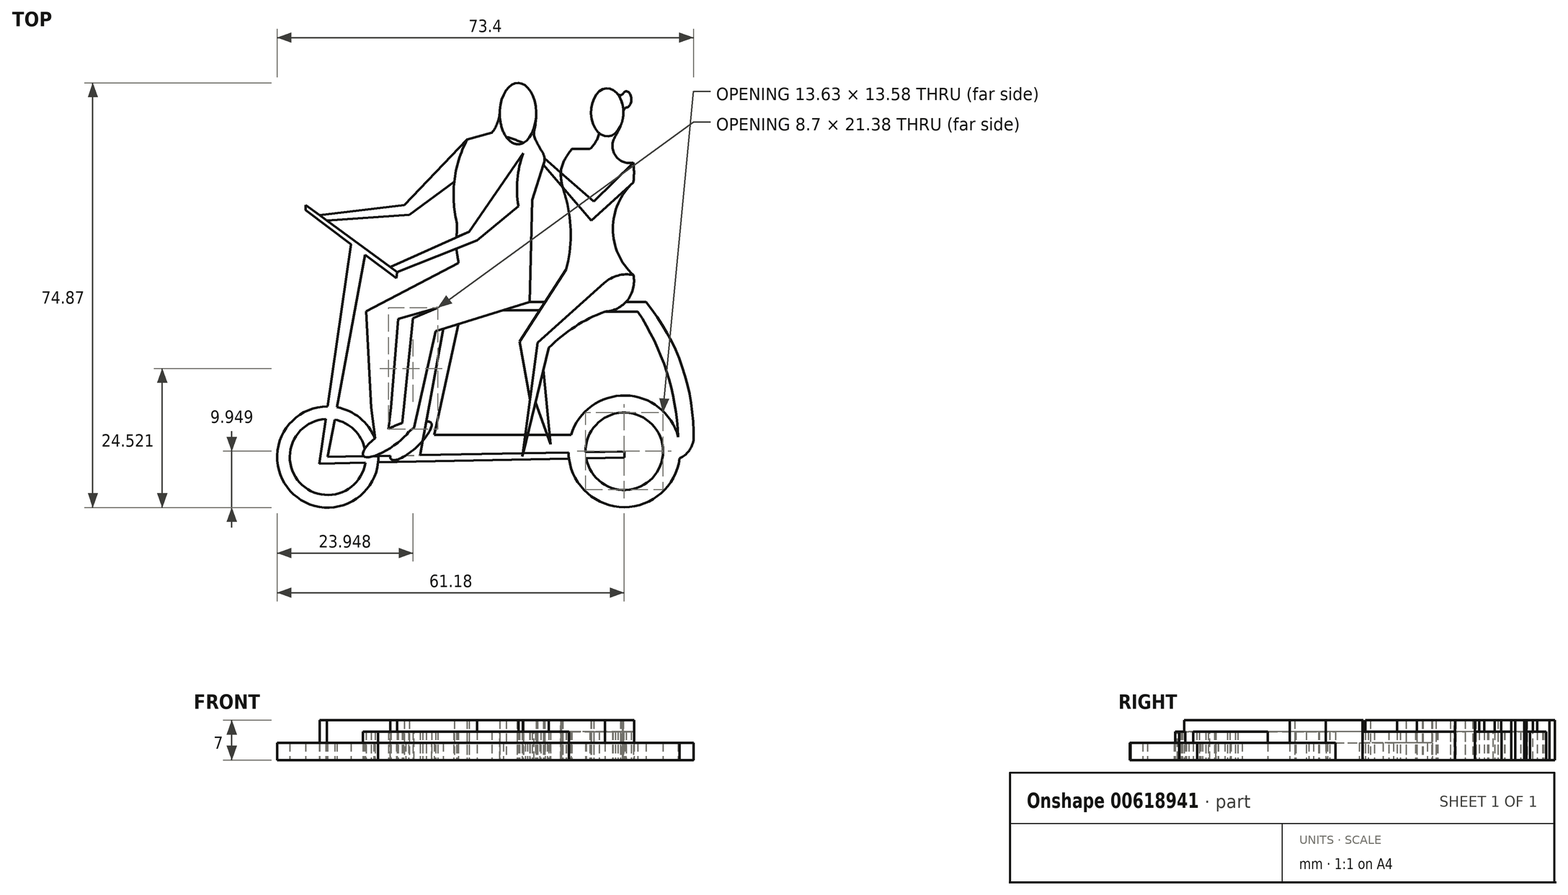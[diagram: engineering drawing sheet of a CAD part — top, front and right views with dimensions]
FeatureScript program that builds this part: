
annotation { "Feature Type Name" : "Feature", "Feature Type Description" : "" }
export const myFeature = defineFeature(function(context is Context, id is Id, definition is map)
    precondition{}
    {
        {
            var Q0;
            Q0=qCreatedBy(makeId("Top.planeOp"),FACE);
            var sketch = newSketch(context, id + "F0", { "sketchPlane" : qUnion([Q0])});
            skLineSegment(sketch, "E0", {"start": v(-116.6, -48.98) * mm, "end": v(-114.7, -48.98) * mm});
            skArc(sketch, "E1", {"start": v(-94.37, -13.85) * mm, "mid": v(-94.25, -12.1) * mm, "end": v(-94.37, -10.37) * mm});
            skArc(sketch, "E2", {"start": v(-97.5, -5.68) * mm, "mid": v(-97.53, -9.1) * mm, "end": v(-94.37, -10.37) * mm});
            skLineSegment(sketch, "E3", {"start": v(-97.5, -5.68) * mm, "end": v(-100.18, -3.95) * mm});
            skPoint(sketch, "E4.startSnap0", {"position": v(-116.27, -23.85) * mm});
            skPoint(sketch, "E5.startSnap0", {"position": v(-110.08, -34.92) * mm});
            skPoint(sketch, "E6.endSnap0", {"position": v(-97.53, -9.1) * mm});
            skArc(sketch, "E7", {"start": v(-99.4, -36.63) * mm, "mid": v(-95.38, -34.57) * mm, "end": v(-94.37, -30.19) * mm});
            skPoint(sketch, "E8.endSnap0", {"position": v(-107.17, -42.99) * mm});
            skPoint(sketch, "E9.startSnap0", {"position": v(-109.77, -40.6) * mm});
            skLineSegment(sketch, "E10", {"start": v(-109.25, -42.99) * mm, "end": v(-113.94, -62.2) * mm});
            skLineSegment(sketch, "E11", {"start": v(-99.5, -31.56) * mm, "end": v(-111.26, -42.09) * mm});
            skLineSegment(sketch, "E12", {"start": v(-111.26, -42.09) * mm, "end": v(-113.94, -62.2) * mm});
            skLineSegment(sketch, "E13", {"start": v(-106.24, -29.19) * mm, "end": v(-114.45, -41.92) * mm});
            skLineSegment(sketch, "E14", {"start": v(-114.45, -41.92) * mm, "end": v(-112.6, -52.14) * mm});
            skLineSegment(sketch, "E15", {"start": v(-111.6, -52.59) * mm, "end": v(-108.96, -60) * mm});
            skLineSegment(sketch, "E16", {"start": v(-108.96, -60) * mm, "end": v(-110.2, -46.86) * mm});
            skLineSegment(sketch, "E17", {"start": v(-101.78, -20.58) * mm, "end": v(-94.37, -13.85) * mm});
            skLineSegment(sketch, "E18", {"start": v(-94.37, -10.37) * mm, "end": v(-101.35, -17.21) * mm});
            skPoint(sketch, "E18.endSnap0", {"position": v(-98.08, -17.21) * mm});
            skLineSegment(sketch, "E19", {"start": v(-101.35, -17.21) * mm, "end": v(-110.02, -9.6) * mm});
            skArc(sketch, "E20", {"start": v(-99.4, -36.63) * mm, "mid": v(-104.67, -39.27) * mm, "end": v(-109.25, -42.99) * mm});
            skArc(sketch, "E21", {"start": v(-94.37, -13.85) * mm, "mid": v(-97.98, -22.02) * mm, "end": v(-94.37, -30.19) * mm});
            skFitSpline(sketch, "E22", {"points": [v(-105.2, -7.94) * mm, v(-107.16, -12.1) * mm, v(-106.18, -16.95) * mm], "startDerivative": vector(-6.26, -8.42) * mm, "endDerivative": vector(2.06, -8.25) * mm});
            skArc(sketch, "E23", {"start": v(-106.24, -29.19) * mm, "mid": v(-105.4, -23.07) * mm, "end": v(-106.18, -16.95) * mm});
            skLineSegment(sketch, "E24", {"start": v(-105.2, -7.94) * mm, "end": v(-102.02, -7.94) * mm});
            skArc(sketch, "E25", {"start": v(-102.02, -7.94) * mm, "mid": v(-100.7, -6.13) * mm, "end": v(-100.18, -3.95) * mm});
            skLineSegment(sketch, "E26", {"start": v(-112.66, -7.26) * mm, "end": v(-113.8, -8.71) * mm});
            skArc(sketch, "E27", {"start": v(-123.67, -6.32) * mm, "mid": v(-125.9, -13.41) * mm, "end": v(-125.5, -20.84) * mm});
            skArc(sketch, "E28", {"start": v(-113.8, -8.71) * mm, "mid": v(-114.89, -14.53) * mm, "end": v(-114.05, -20.4) * mm});
            skFitSpline(sketch, "E29", {"points": [v(-125.5, -20.84) * mm, v(-125.5, -22.87) * mm, v(-125.5, -25.98) * mm, v(-125.5, -30.56) * mm, v(-128, -34.92) * mm], "startDerivative": vector(1.3, -15.74) * mm, "endDerivative": vector(3.93, -16.51) * mm});
            skFitSpline(sketch, "E30", {"points": [v(-114.05, -20.4) * mm, v(-114.4, -23.72) * mm, v(-114.05, -27.05) * mm, v(-114.4, -29.84) * mm, v(-114.05, -34.92) * mm], "startDerivative": vector(0, -14.22) * mm, "endDerivative": vector(0, -18.32) * mm});
            skLineSegment(sketch, "E31", {"start": v(-114.4, -29.84) * mm, "end": v(-133.21, -37.8) * mm});
            skLineSegment(sketch, "E32", {"start": v(-133.21, -37.8) * mm, "end": v(-134.84, -53.98) * mm});
            skLineSegment(sketch, "E33", {"start": v(-132.34, -53.98) * mm, "end": v(-129.2, -40.08) * mm});
            skLineSegment(sketch, "E34", {"start": v(-129.2, -40.08) * mm, "end": v(-112.66, -34.92) * mm});
            skLineSegment(sketch, "E35", {"start": v(-125.18, -28.08) * mm, "end": v(-141.44, -36.6) * mm});
            skLineSegment(sketch, "E36", {"start": v(-141.44, -36.6) * mm, "end": v(-140.6, -53.55) * mm});
            skLineSegment(sketch, "E37", {"start": v(-137.12, -53.55) * mm, "end": v(-135.82, -37.9) * mm});
            skLineSegment(sketch, "E38", {"start": v(-135.82, -37.9) * mm, "end": v(-128.86, -35.96) * mm});
            skArc(sketch, "E39", {"start": v(-112.66, -7.26) * mm, "mid": v(-115.95, -6.08) * mm, "end": v(-119.3, -5.1) * mm});
            skPoint(sketch, "E40.endSnap0", {"position": v(-114.89, -14.53) * mm});
            skLineSegment(sketch, "E41", {"start": v(-112.66, -34.92) * mm, "end": v(-92.15, -34.92) * mm});
            skLineSegment(sketch, "E42", {"start": v(-125.22, -38.84) * mm, "end": v(-129.2, -57.18) * mm});
            skArc(sketch, "E43", {"start": v(-83.78, -59.33) * mm, "mid": v(-85.75, -46.36) * mm, "end": v(-92.15, -34.92) * mm});
            skPoint(sketch, "E44.endSnap0", {"position": v(-145, -40.91) * mm});
            skLineSegment(sketch, "E45", {"start": v(-128.94, -58.34) * mm, "end": v(-113.43, -58.34) * mm});
            skLineSegment(sketch, "E46", {"start": v(-123.67, -6.32) * mm, "end": v(-119.3, -5.1) * mm});
            skLineSegment(sketch, "E47", {"start": v(-152.12, -17.86) * mm, "end": v(-136.02, -29.67) * mm});
            skLineSegment(sketch, "E48", {"start": v(-121.92, -24.08) * mm, "end": v(-136.02, -29.67) * mm});
            skLineSegment(sketch, "E49", {"start": v(-123.32, -22.52) * mm, "end": v(-113.8, -8.71) * mm});
            skLineSegment(sketch, "E50", {"start": v(-149.68, -19.65) * mm, "end": v(-134.77, -17.86) * mm});
            skLineSegment(sketch, "E51", {"start": v(-134.77, -17.86) * mm, "end": v(-123.67, -6.32) * mm});
            skLineSegment(sketch, "E52", {"start": v(-133.87, -19.52) * mm, "end": v(-124.02, -12.3) * mm});
            skCircle(sketch, "E53", {"center": v(-148.23, -62.25) * mm, "radius": 8.92 * mm});
            skCircle(sketch, "E54", {"center": v(-95.96, -61.25) * mm, "radius": 9.84 * mm});
            skLineSegment(sketch, "E55", {"start": v(-148.23, -62.25) * mm, "end": v(-95.96, -61.25) * mm});
            skLineSegment(sketch, "E56", {"start": v(-129.2, -57.18) * mm, "end": v(-129.45, -58.34) * mm});
            skLineSegment(sketch, "E57", {"start": v(-129.45, -58.34) * mm, "end": v(-128.94, -58.34) * mm});
            skArc(sketch, "E58", {"start": v(-89.73, -62.43) * mm, "mid": v(-85.97, -62.39) * mm, "end": v(-83.78, -59.33) * mm});
            skEllipse(sketch, "E59", {"center": v(-114.71, -1.7) * mm, "majorRadius": 5.4 * mm, "minorRadius": 3.2 * mm, "majorAxis": v(0, -1)});
            skArc(sketch, "E60", {"start": v(-119.3, -5.1) * mm, "mid": v(-118.29, -3.24) * mm, "end": v(-117.9, -1.16) * mm});
            skLineSegment(sketch, "E61", {"start": v(-97.98, 0) * mm, "end": v(-97.98, -1.77) * mm});
            skEllipse(sketch, "E62", {"center": v(-98.97, -1.48) * mm, "majorRadius": 4.24 * mm, "minorRadius": 2.85 * mm, "majorAxis": v(0, -1)});
            skEllipse(sketch, "E63", {"center": v(-95.61, 0.8) * mm, "majorRadius": 1.42 * mm, "minorRadius": 0.88 * mm, "majorAxis": v(0, -1)});
            skArc(sketch, "E64", {"start": v(-97.1, 1.72) * mm, "mid": v(-96.52, 1.56) * mm, "end": v(-96.1, 1.99) * mm});
            skArc(sketch, "E65", {"start": v(-95.61, -0.63) * mm, "mid": v(-96.04, -1.07) * mm, "end": v(-96.12, -1.7) * mm});
            skPoint(sketch, "E66.2.internal.snap0", {"position": v(-94.73, 0.8) * mm});
            skArc(sketch, "E67", {"start": v(-95.54, -5.6) * mm, "mid": v(-96.7, -5.3) * mm, "end": v(-97.9, -5.42) * mm});
            skLineSegment(sketch, "E68", {"start": v(-149.75, -63.42) * mm, "end": v(-95.96, -62.33) * mm});
            skLineSegment(sketch, "E69", {"start": v(-95.96, -62.33) * mm, "end": v(-95.96, -61.25) * mm});
            skLineSegment(sketch, "E70", {"start": v(-152.12, -17.86) * mm, "end": v(-152.12, -18.73) * mm});
            skLineSegment(sketch, "E71", {"start": v(-152.12, -18.73) * mm, "end": v(-136.11, -30.76) * mm});
            skLineSegment(sketch, "E72", {"start": v(-136.11, -30.76) * mm, "end": v(-136.02, -29.67) * mm});
            skCircle(sketch, "E73", {"center": v(-148.23, -62.25) * mm, "radius": 6.7 * mm});
            skCircle(sketch, "E74", {"center": v(-95.96, -61.25) * mm, "radius": 6.83 * mm});
            skLineSegment(sketch, "E75", {"start": v(-137.24, -28.77) * mm, "end": v(-123.32, -22.52) * mm});
            skLineSegment(sketch, "E76", {"start": v(-133.87, -19.52) * mm, "end": v(-148.42, -20.57) * mm});
            skLineSegment(sketch, "E77", {"start": v(-113, -58.34) * mm, "end": v(-105.36, -58.34) * mm});
            skLineSegment(sketch, "E78", {"start": v(-148.23, -62.25) * mm, "end": v(-141.66, -26.59) * mm});
            skLineSegment(sketch, "E79", {"start": v(-149.75, -63.42) * mm, "end": v(-144.11, -24.74) * mm});
            skLineSegment(sketch, "E80", {"start": v(-110.02, -10.17) * mm, "end": v(-112.2, -16.92) * mm});
            skLineSegment(sketch, "E81", {"start": v(-112.2, -16.92) * mm, "end": v(-112.66, -34.92) * mm});
            skArc(sketch, "E82", {"start": v(-110.02, -10.17) * mm, "mid": v(-110.68, -8.12) * mm, "end": v(-112.66, -7.26) * mm});
            skLineSegment(sketch, "E83", {"start": v(-101.78, -20.58) * mm, "end": v(-110.2, -10.75) * mm});
            skLineSegment(sketch, "E84", {"start": v(-117.29, -36.37) * mm, "end": v(-110.86, -36.37) * mm});
            skLineSegment(sketch, "E85", {"start": v(-99.4, -36.63) * mm, "end": v(-93.58, -36.63) * mm});
            skArc(sketch, "E86", {"start": v(-86.46, -58.72) * mm, "mid": v(-88.51, -47.19) * mm, "end": v(-93.58, -36.63) * mm});
            skLineSegment(sketch, "E87", {"start": v(-127.85, -39.66) * mm, "end": v(-131.96, -61.94) * mm});
            skArc(sketch, "E88", {"start": v(-94.37, -30.19) * mm, "mid": v(-97.1, -30.26) * mm, "end": v(-99.5, -31.56) * mm});
            skLineSegment(sketch, "E89", {"start": v(-121.92, -24.08) * mm, "end": v(-114.63, -18) * mm});
            skFitSpline(sketch, "E90", {"points": [v(-111.52, -2.3) * mm, v(-111.87, -5.2) * mm, v(-111.54, -6.5) * mm, v(-110.68, -8.12) * mm], "startDerivative": vector(-0.02, -8.02) * mm, "endDerivative": vector(2.84, -6.3) * mm});
            skArc(sketch, "E91", {"start": v(-97.5, -5.68) * mm, "mid": v(-96.9, -4.5) * mm, "end": v(-96.38, -3.27) * mm});
            skLineSegment(sketch, "E92", {"start": v(-140.6, -53.55) * mm, "end": v(-139.84, -59.24) * mm});
            skLineSegment(sketch, "E93", {"start": v(-137.12, -53.55) * mm, "end": v(-137.78, -59.24) * mm});
            skLineSegment(sketch, "E94", {"start": v(-134.84, -53.98) * mm, "end": v(-135.53, -59.19) * mm});
            skLineSegment(sketch, "E95", {"start": v(-132.34, -53.98) * mm, "end": v(-133.57, -59.41) * mm});
            skPoint(sketch, "E96.0.internal.snap0", {"position": v(-134.27, -61.65) * mm});
            skEllipse(sketch, "E97", {"center": v(-133.57, -59.41) * mm, "majorRadius": 4.77 * mm, "minorRadius": 1.46 * mm, "majorAxis": v(-0.73, -0.68)});
            skEllipse(sketch, "E98", {"center": v(-137.78, -59.24) * mm, "majorRadius": 5.05 * mm, "minorRadius": 1.5 * mm, "majorAxis": v(-0.83, -0.55)});
            skArc(sketch, "E99", {"start": v(-107.16, -12.1) * mm, "mid": v(-107.07, -13.42) * mm, "end": v(-106.8, -14.72) * mm});
            skSolve(sketch);
        }
        {
            var Q0;
            {var subQ0=sQuery(id+"F0.wireOp",EDGE,"E79");var subQ1=sQuery(id+"F0.wireOp",EDGE,"E53");var subQ2=makeQuery(id+"F0.imprint","INTERSECT",VERTEX,{"derivedFrom":[subQ1,subQ0]});Q0=makeQuery(id+"F0.imprint","IMPRINT",FACE,{"disambiguationData":[TD([[makeQuery(id+"F0.imprint","IMPRINT",EDGE,{"disambiguationData":[TD([[subQ2,1.0]])],"derivedFrom":subQ1}),-1.0]])]});}
            var Q1;
            {var subQ0=sQuery(id+"F0.wireOp",EDGE,"E79");var subQ1=sQuery(id+"F0.wireOp",EDGE,"E53");var subQ2=makeQuery(id+"F0.imprint","INTERSECT",VERTEX,{"derivedFrom":[subQ1,subQ0]});Q1=makeQuery(id+"F0.imprint","IMPRINT",FACE,{"disambiguationData":[TD([[makeQuery(id+"F0.imprint","IMPRINT",EDGE,{"disambiguationData":[TD([[subQ2,1.0]])],"derivedFrom":subQ1}),1.0]])]});}
            var Q2;
            {var subQ0=sQuery(id+"F0.wireOp",EDGE,"E79");var subQ1=sQuery(id+"F0.wireOp",EDGE,"E53");var subQ2=makeQuery(id+"F0.imprint","INTERSECT",VERTEX,{"derivedFrom":[subQ1,subQ0]});Q2=makeQuery(id+"F0.imprint","IMPRINT",FACE,{"disambiguationData":[TD([[makeQuery(id+"F0.imprint","IMPRINT",EDGE,{"disambiguationData":[TD([[subQ2,-1.0]])],"derivedFrom":subQ1}),1.0]])]});}
            var Q3;
            {var subQ0=sQuery(id+"F0.wireOp",EDGE,"E78");var subQ1=sQuery(id+"F0.wireOp",EDGE,"E53");var subQ2=makeQuery(id+"F0.imprint","INTERSECT",VERTEX,{"derivedFrom":[subQ1,subQ0]});Q3=makeQuery(id+"F0.imprint","IMPRINT",FACE,{"disambiguationData":[TD([[makeQuery(id+"F0.imprint","IMPRINT",EDGE,{"disambiguationData":[TD([[subQ2,1.0]])],"derivedFrom":subQ1}),1.0]])]});}
            var Q4;
            {var subQ1=sQuery(id+"F0.wireOp",EDGE,"E55");var subQ7=sQuery(id+"F0.wireOp",EDGE,"E78");var subQ10=makeQuery(id+"F0.imprint","INTERSECT",VERTEX,{"derivedFrom":[subQ1,subQ7]});Q4=makeQuery(id+"F0.imprint","IMPRINT",FACE,{"disambiguationData":[TD([[makeQuery(id+"F0.imprint","IMPRINT",EDGE,{"disambiguationData":[TD([[subQ10,-1.0]])],"derivedFrom":subQ1}),-1.0]])]});}
            var Q5;
            {var subQ0=sQuery(id+"F0.wireOp",EDGE,"E68");var subQ1=sQuery(id+"F0.wireOp",EDGE,"E53");var subQ2=makeQuery(id+"F0.imprint","INTERSECT",VERTEX,{"derivedFrom":[subQ1,subQ0]});Q5=makeQuery(id+"F0.imprint","IMPRINT",FACE,{"disambiguationData":[TD([[makeQuery(id+"F0.imprint","IMPRINT",EDGE,{"disambiguationData":[TD([[subQ2,-1.0]])],"derivedFrom":subQ1}),1.0]])]});}
            var Q6;
            {var subQ7=sQuery(id+"F0.wireOp",EDGE,"E70");Q6=makeQuery(id+"F0.imprint","IMPRINT",FACE,{"disambiguationData":[TD([[makeQuery(id+"F0.imprint","IMPRINT",EDGE,{"derivedFrom":subQ7}),1.0]])]});}
            var Q7;
            {var subQ8=sQuery(id+"F0.wireOp",EDGE,"E10");var subQ10=sQuery(id+"F0.wireOp",EDGE,"E12");var subQ11=makeQuery(id+"F0.imprint","INTERSECT",VERTEX,{"derivedFrom":[subQ8,subQ10]});Q7=makeQuery(id+"F0.imprint","IMPRINT",FACE,{"disambiguationData":[TD([[makeQuery(id+"F0.imprint","IMPRINT",EDGE,{"disambiguationData":[TD([[subQ11,1.0]])],"derivedFrom":subQ8}),1.0]])]});}
            var Q8;
            {var subQ0=sQuery(id+"F0.wireOp",EDGE,"E68");var subQ1=sQuery(id+"F0.wireOp",EDGE,"E54");var subQ2=makeQuery(id+"F0.imprint","INTERSECT",VERTEX,{"derivedFrom":[subQ1,subQ0]});Q8=makeQuery(id+"F0.imprint","IMPRINT",FACE,{"disambiguationData":[TD([[makeQuery(id+"F0.imprint","IMPRINT",EDGE,{"disambiguationData":[TD([[subQ2,1.0]])],"derivedFrom":subQ1}),1.0]])]});}
            var Q9;
            {var subQ0=sQuery(id+"F0.wireOp",EDGE,"E69");Q9=makeQuery(id+"F0.imprint","IMPRINT",FACE,{"disambiguationData":[TD([[makeQuery(id+"F0.imprint","IMPRINT",EDGE,{"derivedFrom":subQ0}),1.0]])]});}
            var Q10;
            {var subQ0=sQuery(id+"F0.wireOp",EDGE,"E54");var subQ9=makeQuery(id+"F0.imprint","INTERSECT",VERTEX,{"derivedFrom":[subQ0,sQuery(id+"F0.wireOp",EDGE,"E77")]});Q10=makeQuery(id+"F0.imprint","IMPRINT",FACE,{"disambiguationData":[TD([[makeQuery(id+"F0.imprint","IMPRINT",EDGE,{"disambiguationData":[TD([[subQ9,1.0]])],"derivedFrom":subQ0}),1.0]])]});}
            var Q11;
            {var subQ0=sQuery(id+"F0.wireOp",EDGE,"E68");var subQ1=sQuery(id+"F0.wireOp",EDGE,"E54");var subQ2=makeQuery(id+"F0.imprint","INTERSECT",VERTEX,{"derivedFrom":[subQ1,subQ0]});Q11=makeQuery(id+"F0.imprint","IMPRINT",FACE,{"disambiguationData":[TD([[makeQuery(id+"F0.imprint","IMPRINT",EDGE,{"disambiguationData":[TD([[subQ2,-1.0]])],"derivedFrom":subQ1}),1.0]])]});}
            var Q12;
            {var subQ4=sQuery(id+"F0.wireOp",EDGE,"E43");Q12=makeQuery(id+"F0.imprint","IMPRINT",FACE,{"disambiguationData":[TD([[makeQuery(id+"F0.imprint","IMPRINT",EDGE,{"derivedFrom":subQ4}),1.0]])]});}
            var Q13;
            {var subQ0=sQuery(id+"F0.wireOp",EDGE,"E84");Q13=makeQuery(id+"F0.imprint","IMPRINT",FACE,{"disambiguationData":[TD([[makeQuery(id+"F0.imprint","IMPRINT",EDGE,{"derivedFrom":subQ0}),1.0]])]});}
            var Q14;
            {var subQ0=sQuery(id+"F0.wireOp",EDGE,"E42");Q14=makeQuery(id+"F0.imprint","IMPRINT",FACE,{"disambiguationData":[TD([[makeQuery(id+"F0.imprint","IMPRINT",EDGE,{"derivedFrom":subQ0}),-1.0]])]});}
            var Q15;
            {var subQ0=sQuery(id+"F0.wireOp",EDGE,"E77");var subQ10=sQuery(id+"F0.wireOp",EDGE,"E10");var subQ11=makeQuery(id+"F0.imprint","INTERSECT",VERTEX,{"derivedFrom":[subQ10,subQ0]});Q15=makeQuery(id+"F0.imprint","IMPRINT",FACE,{"disambiguationData":[TD([[makeQuery(id+"F0.imprint","IMPRINT",EDGE,{"disambiguationData":[TD([[subQ11,-1.0]])],"derivedFrom":subQ10}),1.0]])]});}
            extrude(context, id + "F1", {"entities" : qUnion([Q0, Q1, Q2, Q3, Q4, Q5, Q6, Q7, Q8, Q9, Q10, Q11, Q12, Q13, Q14, Q15]), "depth" : 3 * mm, "offsetDistance" : 25 * mm});
        }
        {
            var Q0;
            {var subQ6=sQuery(id+"F0.wireOp",EDGE,"E26");Q0=makeQuery(id+"F0.imprint","IMPRINT",FACE,{"disambiguationData":[TD([[makeQuery(id+"F0.imprint","IMPRINT",EDGE,{"derivedFrom":subQ6}),-1.0]])]});}
            var Q1;
            {var subQ7=sQuery(id+"F0.wireOp",EDGE,"E35");Q1=makeQuery(id+"F0.imprint","IMPRINT",FACE,{"disambiguationData":[TD([[makeQuery(id+"F0.imprint","IMPRINT",EDGE,{"derivedFrom":subQ7}),1.0]])]});}
            var Q2;
            {var subQ11=sQuery(id+"F0.wireOp",EDGE,"E26");Q2=makeQuery(id+"F0.imprint","IMPRINT",FACE,{"disambiguationData":[TD([[makeQuery(id+"F0.imprint","IMPRINT",EDGE,{"derivedFrom":subQ11}),1.0]])]});}
            var Q3;
            {var subQ0=sQuery(id+"F0.wireOp",EDGE,"E17");Q3=makeQuery(id+"F0.imprint","IMPRINT",FACE,{"disambiguationData":[TD([[makeQuery(id+"F0.imprint","IMPRINT",EDGE,{"derivedFrom":subQ0}),-1.0]])]});}
            var Q4;
            {var subQ5=sQuery(id+"F0.wireOp",EDGE,"E2");Q4=makeQuery(id+"F0.imprint","IMPRINT",FACE,{"disambiguationData":[TD([[makeQuery(id+"F0.imprint","IMPRINT",EDGE,{"derivedFrom":subQ5}),-1.0]])]});}
            var Q5;
            {var subQ0=sQuery(id+"F0.wireOp",EDGE,"E14");Q5=makeQuery(id+"F0.imprint","IMPRINT",FACE,{"disambiguationData":[TD([[makeQuery(id+"F0.imprint","IMPRINT",EDGE,{"derivedFrom":subQ0}),1.0]])]});}
            var Q6;
            {var subQ0=sQuery(id+"F0.wireOp",EDGE,"E15");var subQ1=sQuery(id+"F0.wireOp",EDGE,"E10");var subQ2=makeQuery(id+"F0.imprint","INTERSECT",VERTEX,{"derivedFrom":[subQ1,subQ0]});Q6=makeQuery(id+"F0.imprint","IMPRINT",FACE,{"disambiguationData":[TD([[makeQuery(id+"F0.imprint","IMPRINT",EDGE,{"disambiguationData":[TD([[subQ2,1.0]])],"derivedFrom":subQ1}),1.0]])]});}
            var Q7;
            {var subQ0=sQuery(id+"F0.wireOp",EDGE,"E63");var subQ2=sQuery(id+"F0.wireOp",EDGE,"E62");var subQ3=makeQuery(id+"F0.imprint","INTERSECT",VERTEX,{"disambiguationData":[OD(0.0)],"derivedFrom":[subQ2,subQ0]});Q7=makeQuery(id+"F0.imprint","IMPRINT",FACE,{"disambiguationData":[TD([[makeQuery(id+"F0.imprint","IMPRINT",EDGE,{"disambiguationData":[TD([[subQ3,-1.0]])],"derivedFrom":subQ2}),-1.0]])]});}
            var Q8;
            {var subQ0=sQuery(id+"F0.wireOp",EDGE,"E65");var subQ1=sQuery(id+"F0.wireOp",EDGE,"E62");var subQ2=makeQuery(id+"F0.imprint","INTERSECT",VERTEX,{"disambiguationData":[OD(1.0)],"derivedFrom":[subQ1,subQ0]});Q8=makeQuery(id+"F0.imprint","IMPRINT",FACE,{"disambiguationData":[TD([[makeQuery(id+"F0.imprint","IMPRINT",EDGE,{"disambiguationData":[TD([[subQ2,-1.0]])],"derivedFrom":subQ1}),-1.0]])]});}
            var Q9;
            {var subQ0=sQuery(id+"F0.wireOp",EDGE,"E64");var subQ1=sQuery(id+"F0.wireOp",EDGE,"E62");var subQ2=makeQuery(id+"F0.imprint","INTERSECT",VERTEX,{"derivedFrom":[subQ1,subQ0]});Q9=makeQuery(id+"F0.imprint","IMPRINT",FACE,{"disambiguationData":[TD([[makeQuery(id+"F0.imprint","IMPRINT",EDGE,{"disambiguationData":[TD([[subQ2,1.0]])],"derivedFrom":subQ1}),-1.0]])]});}
            var Q10;
            {var subQ0=sQuery(id+"F0.wireOp",EDGE,"E67");var subQ3=sQuery(id+"F0.wireOp",EDGE,"E91");var subQ5=makeQuery(id+"F0.imprint","INTERSECT",VERTEX,{"derivedFrom":[subQ0,subQ3]});Q10=makeQuery(id+"F0.imprint","IMPRINT",FACE,{"disambiguationData":[TD([[makeQuery(id+"F0.imprint","IMPRINT",EDGE,{"disambiguationData":[TD([[subQ5,-1.0]])],"derivedFrom":subQ3}),1.0]])]});}
            var Q11;
            {var subQ0=sQuery(id+"F0.wireOp",EDGE,"E91");var subQ3=sQuery(id+"F0.wireOp",EDGE,"E67");var subQ5=makeQuery(id+"F0.imprint","INTERSECT",VERTEX,{"derivedFrom":[subQ3,subQ0]});Q11=makeQuery(id+"F0.imprint","IMPRINT",FACE,{"disambiguationData":[TD([[makeQuery(id+"F0.imprint","IMPRINT",EDGE,{"disambiguationData":[TD([[subQ5,-1.0]])],"derivedFrom":subQ3}),1.0]])]});}
            var Q12;
            {var subQ0=sQuery(id+"F0.wireOp",EDGE,"E60");var subQ3=sQuery(id+"F0.wireOp",EDGE,"E59");var subQ5=makeQuery(id+"F0.imprint","INTERSECT",VERTEX,{"disambiguationData":[OD(1.0)],"derivedFrom":[subQ3,subQ0]});Q12=makeQuery(id+"F0.imprint","IMPRINT",FACE,{"disambiguationData":[TD([[makeQuery(id+"F0.imprint","IMPRINT",EDGE,{"disambiguationData":[TD([[subQ5,-1.0]])],"derivedFrom":subQ3}),-1.0]])]});}
            var Q13;
            {var subQ5=sQuery(id+"F0.wireOp",EDGE,"E90");Q13=makeQuery(id+"F0.imprint","IMPRINT",FACE,{"disambiguationData":[TD([[makeQuery(id+"F0.imprint","IMPRINT",EDGE,{"derivedFrom":subQ5}),-1.0]])]});}
            var Q14;
            {var subQ0=sQuery(id+"F0.wireOp",EDGE,"E98");var subQ1=sQuery(id+"F0.wireOp",EDGE,"E55");var subQ2=makeQuery(id+"F0.imprint","INTERSECT",VERTEX,{"disambiguationData":[OD(0.0)],"derivedFrom":[subQ1,subQ0]});Q14=makeQuery(id+"F0.imprint","IMPRINT",FACE,{"disambiguationData":[TD([[makeQuery(id+"F0.imprint","IMPRINT",EDGE,{"disambiguationData":[TD([[subQ2,-1.0]])],"derivedFrom":subQ1}),1.0]])]});}
            var Q15;
            {var subQ0=sQuery(id+"F0.wireOp",EDGE,"E73");var subQ1=sQuery(id+"F0.wireOp",EDGE,"E55");var subQ2=makeQuery(id+"F0.imprint","INTERSECT",VERTEX,{"derivedFrom":[subQ1,subQ0]});Q15=makeQuery(id+"F0.imprint","IMPRINT",FACE,{"disambiguationData":[TD([[makeQuery(id+"F0.imprint","IMPRINT",EDGE,{"disambiguationData":[TD([[subQ2,-1.0]])],"derivedFrom":subQ1}),-1.0]])]});}
            var Q16;
            {var subQ0=sQuery(id+"F0.wireOp",EDGE,"E98");var subQ1=sQuery(id+"F0.wireOp",EDGE,"E55");var subQ2=makeQuery(id+"F0.imprint","INTERSECT",VERTEX,{"disambiguationData":[OD(0.0)],"derivedFrom":[subQ1,subQ0]});Q16=makeQuery(id+"F0.imprint","IMPRINT",FACE,{"disambiguationData":[TD([[makeQuery(id+"F0.imprint","IMPRINT",EDGE,{"disambiguationData":[TD([[subQ2,-1.0]])],"derivedFrom":subQ1}),-1.0]])]});}
            var Q17;
            {var subQ0=sQuery(id+"F0.wireOp",EDGE,"E97");var subQ1=sQuery(id+"F0.wireOp",EDGE,"E55");var subQ10=makeQuery(id+"F0.imprint","INTERSECT",VERTEX,{"disambiguationData":[OD(0.0)],"derivedFrom":[subQ1,subQ0]});Q17=makeQuery(id+"F0.imprint","IMPRINT",FACE,{"disambiguationData":[TD([[makeQuery(id+"F0.imprint","IMPRINT",EDGE,{"disambiguationData":[TD([[subQ10,-1.0]])],"derivedFrom":subQ1}),1.0]])]});}
            var Q18;
            {var subQ0=sQuery(id+"F0.wireOp",EDGE,"E97");var subQ1=sQuery(id+"F0.wireOp",EDGE,"E55");var subQ2=makeQuery(id+"F0.imprint","INTERSECT",VERTEX,{"disambiguationData":[OD(0.0)],"derivedFrom":[subQ1,subQ0]});Q18=makeQuery(id+"F0.imprint","IMPRINT",FACE,{"disambiguationData":[TD([[makeQuery(id+"F0.imprint","IMPRINT",EDGE,{"disambiguationData":[TD([[subQ2,-1.0]])],"derivedFrom":subQ1}),-1.0]])]});}
            var Q19;
            {var subQ0=sQuery(id+"F0.wireOp",EDGE,"E97");var subQ1=sQuery(id+"F0.wireOp",EDGE,"E87");var subQ2=makeQuery(id+"F0.imprint","INTERSECT",VERTEX,{"disambiguationData":[OD(0.0)],"derivedFrom":[subQ1,subQ0]});Q19=makeQuery(id+"F0.imprint","IMPRINT",FACE,{"disambiguationData":[TD([[makeQuery(id+"F0.imprint","IMPRINT",EDGE,{"disambiguationData":[TD([[subQ2,-1.0]])],"derivedFrom":subQ1}),1.0]])]});}
            var Q20;
            {var subQ0=sQuery(id+"F0.wireOp",EDGE,"E92");var subQ1=sQuery(id+"F0.wireOp",EDGE,"E53");var subQ2=makeQuery(id+"F0.imprint","INTERSECT",VERTEX,{"derivedFrom":[subQ1,subQ0]});Q20=makeQuery(id+"F0.imprint","IMPRINT",FACE,{"disambiguationData":[TD([[makeQuery(id+"F0.imprint","IMPRINT",EDGE,{"disambiguationData":[TD([[subQ2,-1.0]])],"derivedFrom":subQ1}),-1.0]])]});}
            var Q21;
            {var subQ0=sQuery(id+"F0.wireOp",EDGE,"E16");var subQ1=sQuery(id+"F0.wireOp",EDGE,"E15");var subQ2=makeQuery(id+"F0.imprint","INTERSECT",VERTEX,{"derivedFrom":[subQ1,subQ0]});Q21=makeQuery(id+"F0.imprint","IMPRINT",FACE,{"disambiguationData":[TD([[makeQuery(id+"F0.imprint","IMPRINT",EDGE,{"disambiguationData":[TD([[subQ2,1.0]])],"derivedFrom":subQ1}),1.0]])]});}
            var Q22;
            {var subQ5=sQuery(id+"F0.wireOp",EDGE,"E53");var subQ8=makeQuery(id+"F0.imprint","INTERSECT",VERTEX,{"derivedFrom":[subQ5,sQuery(id+"F0.wireOp",EDGE,"E92")]});Q22=makeQuery(id+"F0.imprint","IMPRINT",FACE,{"disambiguationData":[TD([[makeQuery(id+"F0.imprint","IMPRINT",EDGE,{"disambiguationData":[TD([[subQ8,1.0]])],"derivedFrom":subQ5}),1.0]])]});}
            var Q23;
            {var subQ0=sQuery(id+"F0.wireOp",EDGE,"E98");var subQ1=sQuery(id+"F0.wireOp",EDGE,"E97");var subQ2=makeQuery(id+"F0.imprint","INTERSECT",VERTEX,{"disambiguationData":[OD(0.0)],"derivedFrom":[subQ1,subQ0]});Q23=makeQuery(id+"F0.imprint","IMPRINT",FACE,{"disambiguationData":[TD([[makeQuery(id+"F0.imprint","IMPRINT",EDGE,{"disambiguationData":[TD([[subQ2,-1.0]])],"derivedFrom":subQ1}),1.0]])]});}
            var Q24;
            {var subQ4=sQuery(id+"F0.wireOp",EDGE,"E92");var subQ5=sQuery(id+"F0.wireOp",EDGE,"E53");var subQ6=makeQuery(id+"F0.imprint","INTERSECT",VERTEX,{"derivedFrom":[subQ5,subQ4]});Q24=makeQuery(id+"F0.imprint","IMPRINT",FACE,{"disambiguationData":[TD([[makeQuery(id+"F0.imprint","IMPRINT",EDGE,{"disambiguationData":[TD([[subQ6,1.0]])],"derivedFrom":subQ5}),-1.0]])]});}
            extrude(context, id + "F2", {"entities" : qUnion([Q0, Q1, Q2, Q3, Q4, Q5, Q6, Q7, Q8, Q9, Q10, Q11, Q12, Q13, Q14, Q15, Q16, Q17, Q18, Q19, Q20, Q21, Q22, Q23, Q24]), "depth" : 5 * mm, "offsetDistance" : 25 * mm});
        }
        {
            var Q0;
            {var subQ12=sQuery(id+"F0.wireOp",EDGE,"E20");Q0=makeQuery(id+"F0.imprint","IMPRINT",FACE,{"disambiguationData":[TD([[makeQuery(id+"F0.imprint","IMPRINT",EDGE,{"derivedFrom":subQ12}),-1.0]])]});}
            var Q1;
            {var subQ0=sQuery(id+"F0.wireOp",EDGE,"E88");Q1=makeQuery(id+"F0.imprint","IMPRINT",FACE,{"disambiguationData":[TD([[makeQuery(id+"F0.imprint","IMPRINT",EDGE,{"derivedFrom":subQ0}),1.0]])]});}
            var Q2;
            Q2=makeQuery(id+"F0.imprint","IMPRINT",FACE,{"disambiguationData":[TD([[makeQuery(id+"F0.imprint","IMPRINT",EDGE,{"derivedFrom":sQuery(id+"F0.wireOp",EDGE,"E1")}),1.0]])]});
            var Q3;
            {var subQ0=sQuery(id+"F0.wireOp",EDGE,"E82");var subQ1=sQuery(id+"F0.wireOp",EDGE,"E19");var subQ2=makeQuery(id+"F0.imprint","INTERSECT",VERTEX,{"derivedFrom":[subQ1,subQ0]});Q3=makeQuery(id+"F0.imprint","IMPRINT",FACE,{"disambiguationData":[TD([[makeQuery(id+"F0.imprint","IMPRINT",EDGE,{"disambiguationData":[TD([[subQ2,1.0]])],"derivedFrom":subQ1}),1.0]])]});}
            var Q4;
            {var subQ0=sQuery(id+"F0.wireOp",EDGE,"E49");Q4=makeQuery(id+"F0.imprint","IMPRINT",FACE,{"disambiguationData":[TD([[makeQuery(id+"F0.imprint","IMPRINT",EDGE,{"derivedFrom":subQ0}),-1.0]])]});}
            var Q5;
            {var subQ0=sQuery(id+"F0.wireOp",EDGE,"E75");var subQ1=sQuery(id+"F0.wireOp",EDGE,"E29");var subQ2=makeQuery(id+"F0.imprint","INTERSECT",VERTEX,{"derivedFrom":[subQ1,subQ0]});Q5=makeQuery(id+"F0.imprint","IMPRINT",FACE,{"disambiguationData":[TD([[makeQuery(id+"F0.imprint","IMPRINT",EDGE,{"disambiguationData":[TD([[subQ2,-1.0]])],"derivedFrom":subQ1}),-1.0]])]});}
            var Q6;
            {var subQ2=sQuery(id+"F0.wireOp",EDGE,"E50");Q6=makeQuery(id+"F0.imprint","IMPRINT",FACE,{"disambiguationData":[TD([[makeQuery(id+"F0.imprint","IMPRINT",EDGE,{"derivedFrom":subQ2}),-1.0]])]});}
            var Q7;
            {var subQ1=sQuery(id+"F0.wireOp",EDGE,"E59");var subQ3=sQuery(id+"F0.wireOp",EDGE,"E39");var subQ5=makeQuery(id+"F0.imprint","INTERSECT",VERTEX,{"disambiguationData":[OD(0.0)],"derivedFrom":[subQ3,subQ1]});Q7=makeQuery(id+"F0.imprint","IMPRINT",FACE,{"disambiguationData":[TD([[makeQuery(id+"F0.imprint","IMPRINT",EDGE,{"disambiguationData":[TD([[subQ5,-1.0]])],"derivedFrom":subQ3}),-1.0]])]});}
            var Q8;
            {var subQ3=sQuery(id+"F0.wireOp",EDGE,"E3");var subQ8=sQuery(id+"F0.wireOp",EDGE,"E25");var subQ9=makeQuery(id+"F0.imprint","INTERSECT",VERTEX,{"derivedFrom":[subQ3,subQ8]});Q8=makeQuery(id+"F0.imprint","IMPRINT",FACE,{"disambiguationData":[TD([[makeQuery(id+"F0.imprint","IMPRINT",EDGE,{"disambiguationData":[TD([[subQ9,1.0]])],"derivedFrom":subQ3}),-1.0]])]});}
            var Q9;
            {var subQ0=sQuery(id+"F0.wireOp",EDGE,"E25");var subQ1=sQuery(id+"F0.wireOp",EDGE,"E3");var subQ2=makeQuery(id+"F0.imprint","INTERSECT",VERTEX,{"derivedFrom":[subQ1,subQ0]});Q9=makeQuery(id+"F0.imprint","IMPRINT",FACE,{"disambiguationData":[TD([[makeQuery(id+"F0.imprint","IMPRINT",EDGE,{"disambiguationData":[TD([[subQ2,1.0]])],"derivedFrom":subQ1}),1.0]])]});}
            extrude(context, id + "F3", {"entities" : qUnion([Q0, Q1, Q2, Q3, Q4, Q5, Q6, Q7, Q8, Q9]), "depth" : 7 * mm, "offsetDistance" : 25 * mm});
        }
    });
